# Revit family: ASSA_ABLOY_VersaMax_SA_FBO02
name_source: partatom
category: Doors
units: mm (PartAtom-declared; Revit-internal decimal feet)

## family parameters
Always vertical = Yes
Cut with Voids When Loaded = No
Host = Wall
OmniClass Number = 23.30.10.00
OmniClass Title = Doors
Room Calculation Point = No
Shared = No

## types (3) — shared parameters
Analytic Construction = <None>
BIMobject category = Sliding Doors
Bottom Profile Height = Versamax Leaf : 4"
Bottom Profile Option 01 = Versamax Leaf : 4"
Bottom Profile Option 02 = Versamax Leaf : 5"
Bottom Profile Option 03 = Versamax Leaf : 7"
Brass Polished Finish = Brass, Polished
Brass Satin Finish = Brass, Satin
Clear Anodized = Clear Anodized
Dark Bronze Anodized = Dark Bronze Anodized
Date of publishing = 2015-02-23
Depth = 0.00
Edition number = 1
Frame Material = Clear Anodized
Function = Interior
Glass = Glass
Header = 5 "
Height = 84 "
IFC Classification = Door
Manufacturer name = ASSA ABLOY Entrance Systems-North America
Material main = Aluminium
NBS Reference Code = 25-30-20-77
NBS Reference Description = Sliding Doorset Systems
Nominal height = 0.00
Nominal width = 0.00
Product SKU = VersaMax_SM
Product data url = http://besam-na.bimobject.com
Product family = ICU
Product group = Surface Mount
QR code = http://besam-na.bimobject.com
Rough Height = 89 "
Rubber = Rubber, Black
Slide Leaf Height = 84 "
Stainless Steel Polished Finish = Stainless Steel, Polished
Stainless Steel Satin Finish = Stainless Steel, Satin
Thickness = 5 "
UNSPSC Code = 301715
Uniclass 1.4 Code = L4133
Uniclass 1.4 Description = Sliding
Uniclass 2.0 Code = SS-25-30-20-77
Uniclass 2.0 Description = Sliding Doorset Systems
Wall Closure = By host
Weight Net (Kg) = 0

## per-type parameters (varying)
| type | Frame Width | Slide Leaf Width | Width |
| 36" | 78 " | 38 " | 36 " |
| 42" | 90 " | 44 " | 42 " |
| 48" | 102 " | 50 " | 48 " |

## geometry (parser evidence)
native form markers: Blend x2, Sweep x24
no freeform markers — native parametric forms only
